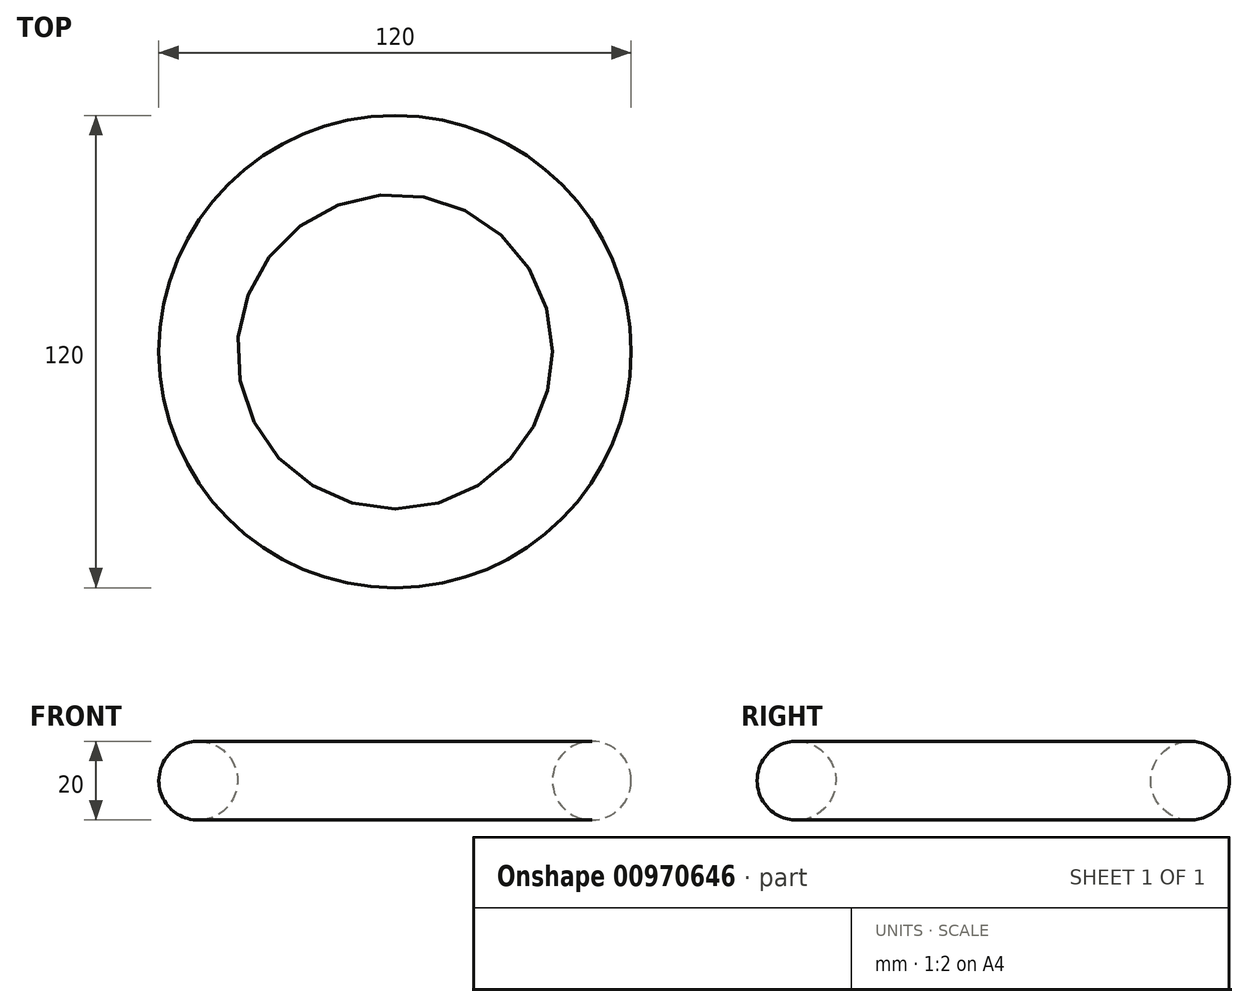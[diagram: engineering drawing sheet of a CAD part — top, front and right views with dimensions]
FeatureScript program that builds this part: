
annotation { "Feature Type Name" : "Feature", "Feature Type Description" : "" }
export const myFeature = defineFeature(function(context is Context, id is Id, definition is map)
    precondition{}
    {
        {
            var Q0;
            Q0=qCreatedBy(makeId("Front.planeOp"),FACE);
            var sketch = newSketch(context, id + "F0", { "sketchPlane" : qUnion([Q0])});
            skLineSegment(sketch, "E0.bottom", {"start": v(0, 0) * mm, "end": v(50, 0) * mm});
            skLineSegment(sketch, "E0.top", {"start": v(0, 10) * mm, "end": v(50, 10) * mm});
            skLineSegment(sketch, "E0.left", {"start": v(0, 0) * mm, "end": v(0, 10) * mm});
            skLineSegment(sketch, "E0.right", {"start": v(50, 0) * mm, "end": v(50, 10) * mm});
            skCircle(sketch, "E1", {"center": v(50, 10) * mm, "radius": 10 * mm});
            skLineSegment(sketch, "E2", {"start": v(0, 5) * mm, "end": v(0, 15) * mm});
            skLineSegment(sketch, "E3.bottom", {"start": v(0, 15) * mm, "end": v(50, 15) * mm});
            skLineSegment(sketch, "E3.top", {"start": v(0, 5) * mm, "end": v(50, 5) * mm});
            skLineSegment(sketch, "E3.left", {"start": v(0, 15) * mm, "end": v(0, 5) * mm});
            skLineSegment(sketch, "E3.right", {"start": v(50, 15) * mm, "end": v(50, 5) * mm});
            skSolve(sketch);
        }
        {
            var Q0;
            {var subQ0=sQuery(id+"F0.wireOp",EDGE,"E3.left");var subQ1=sQuery(id+"F0.wireOp",EDGE,"E0.top");var subQ2=makeQuery(id+"F0.imprint","INTERSECT",VERTEX,{"derivedFrom":[subQ1,subQ0]});Q0=makeQuery(id+"F0.imprint","IMPRINT",FACE,{"disambiguationData":[TD([[makeQuery(id+"F0.imprint","IMPRINT",EDGE,{"disambiguationData":[TD([[subQ2,-1.0]])],"derivedFrom":subQ1}),-1.0]])]});}
            var Q1;
            {var subQ0=sQuery(id+"F0.wireOp",EDGE,"E3.left");var subQ1=sQuery(id+"F0.wireOp",EDGE,"E0.top");var subQ2=makeQuery(id+"F0.imprint","INTERSECT",VERTEX,{"derivedFrom":[subQ1,subQ0]});Q1=makeQuery(id+"F0.imprint","IMPRINT",FACE,{"disambiguationData":[TD([[makeQuery(id+"F0.imprint","IMPRINT",EDGE,{"disambiguationData":[TD([[subQ2,-1.0]])],"derivedFrom":subQ1}),1.0]])]});}
            var Q2;
            {var subQ0=sQuery(id+"F0.wireOp",EDGE,"E3.right");var subQ1=sQuery(id+"F0.wireOp",EDGE,"E0.top");var subQ2=makeQuery(id+"F0.imprint","INTERSECT",VERTEX,{"derivedFrom":[subQ1,subQ0]});Q2=makeQuery(id+"F0.imprint","IMPRINT",FACE,{"disambiguationData":[TD([[makeQuery(id+"F0.imprint","IMPRINT",EDGE,{"disambiguationData":[TD([[subQ2,1.0]])],"derivedFrom":subQ1}),-1.0]])]});}
            var Q3;
            {var subQ0=sQuery(id+"F0.wireOp",EDGE,"E3.right");var subQ1=sQuery(id+"F0.wireOp",EDGE,"E0.top");var subQ2=makeQuery(id+"F0.imprint","INTERSECT",VERTEX,{"derivedFrom":[subQ1,subQ0]});Q3=makeQuery(id+"F0.imprint","IMPRINT",FACE,{"disambiguationData":[TD([[makeQuery(id+"F0.imprint","IMPRINT",EDGE,{"disambiguationData":[TD([[subQ2,1.0]])],"derivedFrom":subQ1}),1.0]])]});}
            var Q4;
            {var subQ4=sQuery(id+"F0.wireOp",EDGE,"E0.right");Q4=makeQuery(id+"F0.imprint","IMPRINT",FACE,{"disambiguationData":[TD([[makeQuery(id+"F0.imprint","IMPRINT",EDGE,{"derivedFrom":subQ4}),-1.0]])]});}
            var Q5;
            {var subQ0=sQuery(id+"F0.wireOp",EDGE,"E0.right");Q5=makeQuery(id+"F0.imprint","IMPRINT",FACE,{"disambiguationData":[TD([[makeQuery(id+"F0.imprint","IMPRINT",EDGE,{"derivedFrom":subQ0}),1.0]])]});}
            var Q6;
            Q6=sQuery(id+"F0.wireOp",EDGE,"E3.left");
            revolve(context, id + "F1", {"surfaceOperationType" : NewSurfaceOperationType.NEW, "entities" : qUnion([Q0, Q1, Q2, Q3, Q4, Q5]), "axis" : qUnion([Q6]), "revolveType" : RevolveType.FULL});
        }
    });
